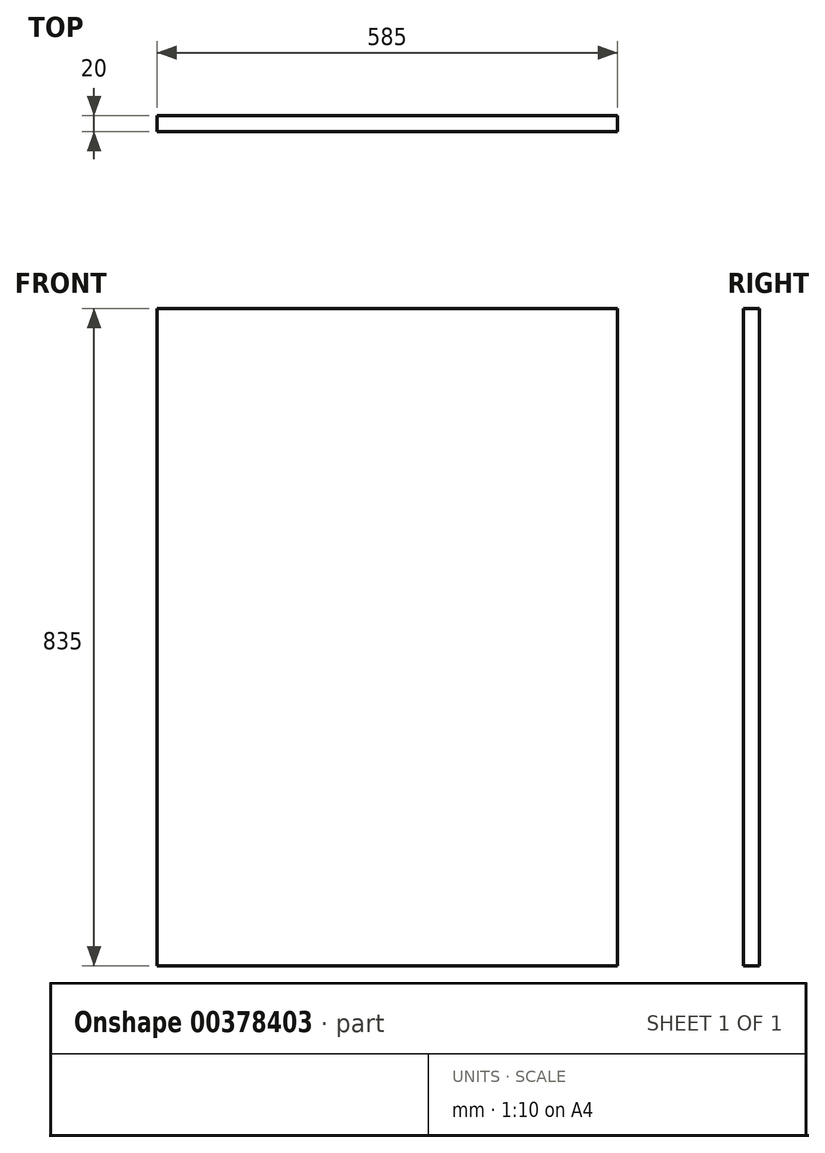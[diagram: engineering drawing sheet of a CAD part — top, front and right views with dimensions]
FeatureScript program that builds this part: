
annotation { "Feature Type Name" : "Feature", "Feature Type Description" : "" }
export const myFeature = defineFeature(function(context is Context, id is Id, definition is map)
    precondition{}
    {
        {
            var Q0;
            Q0=qCreatedBy(makeId("Front.planeOp"),FACE);
            var sketch = newSketch(context, id + "F0", { "sketchPlane" : qUnion([Q0])});
            skLineSegment(sketch, "E0.bottom", {"start": v(292.5, 417.5) * mm, "end": v(-292.5, 417.5) * mm});
            skLineSegment(sketch, "E0.top", {"start": v(292.5, -417.5) * mm, "end": v(-292.5, -417.5) * mm});
            skLineSegment(sketch, "E0.left", {"start": v(292.5, 417.5) * mm, "end": v(292.5, -417.5) * mm});
            skLineSegment(sketch, "E0.right", {"start": v(-292.5, 417.5) * mm, "end": v(-292.5, -417.5) * mm});
            skPoint(sketch, "E0.middle", {"position": v(0, 0) * mm});
            skSolve(sketch);
        }
        {
            var Q0;
            Q0=qSketchRegion(id+"F0",true);
            extrude(context, id + "F1", {"entities" : qUnion([Q0]), "depth" : 20 * mm});
        }
    });
